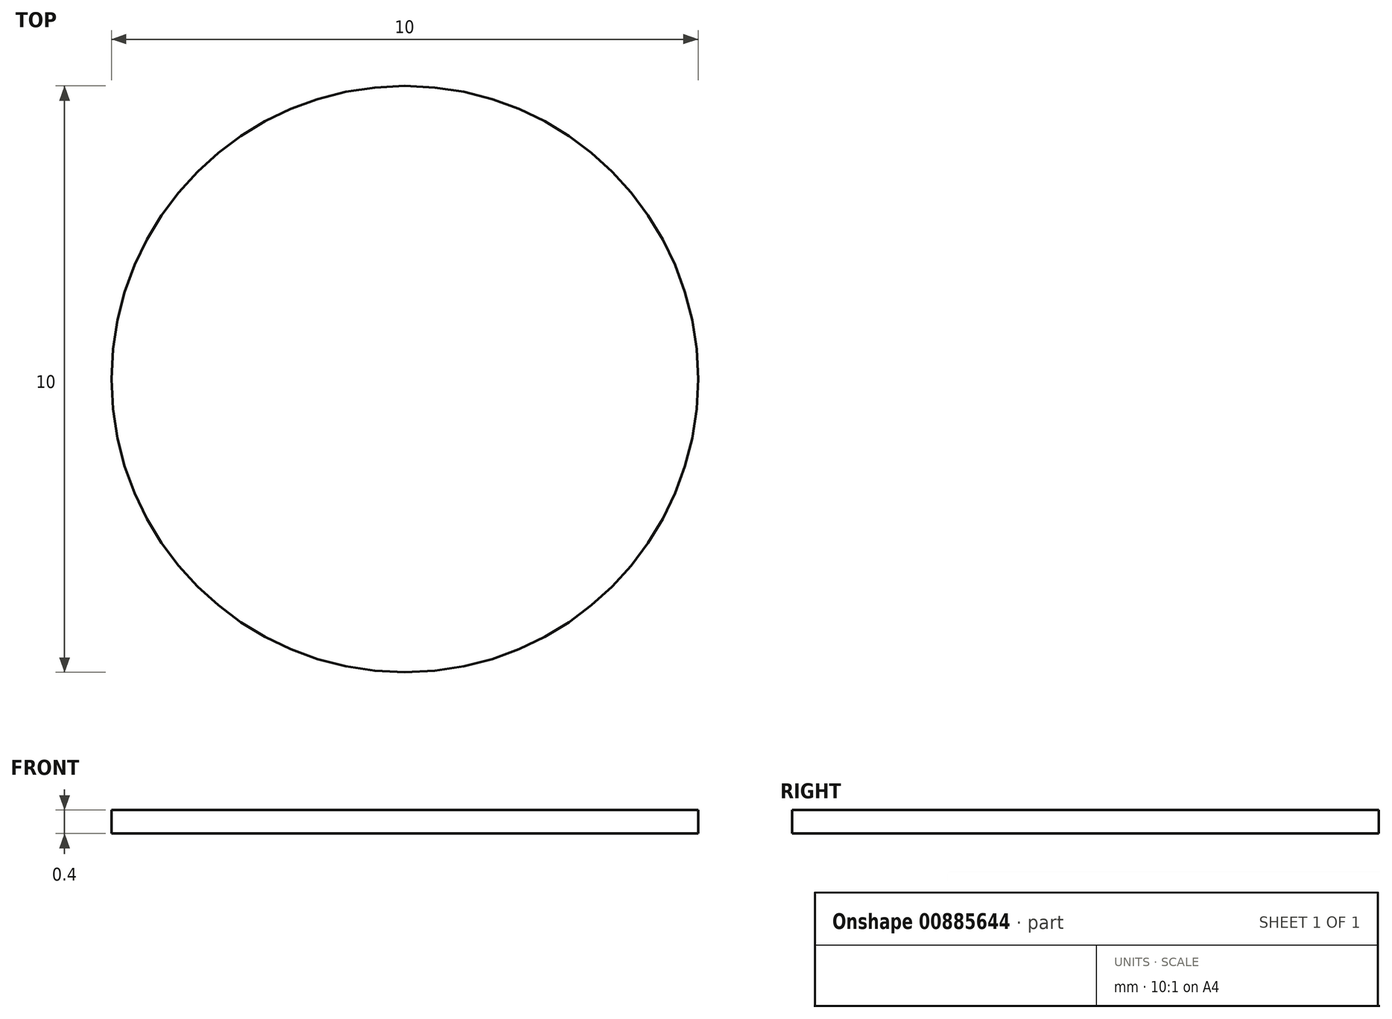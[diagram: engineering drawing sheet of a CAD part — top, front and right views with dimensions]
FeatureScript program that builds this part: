
annotation { "Feature Type Name" : "Feature", "Feature Type Description" : "" }
export const myFeature = defineFeature(function(context is Context, id is Id, definition is map)
    precondition{}
    {
        {
            var Q0;
            Q0=qCreatedBy(makeId("Top.planeOp"),FACE);
            var sketch = newSketch(context, id + "F0", { "sketchPlane" : qUnion([Q0])});
            skCircle(sketch, "E0", {"center": v(0, 0) * mm, "radius": 5 * mm});
            skSolve(sketch);
        }
        {
            var Q0;
            Q0=makeQuery(id+"F0.imprint","IMPRINT",FACE,{"disambiguationData":[TD([[makeQuery(id+"F0.imprint","IMPRINT",EDGE,{"derivedFrom":sQuery(id+"F0.wireOp",EDGE,"E0")}),1.0]])]});
            extrude(context, id + "F1", {"entities" : qUnion([Q0]), "depth" : .4 * mm, "offsetDistance" : 25 * mm});
        }
    });
